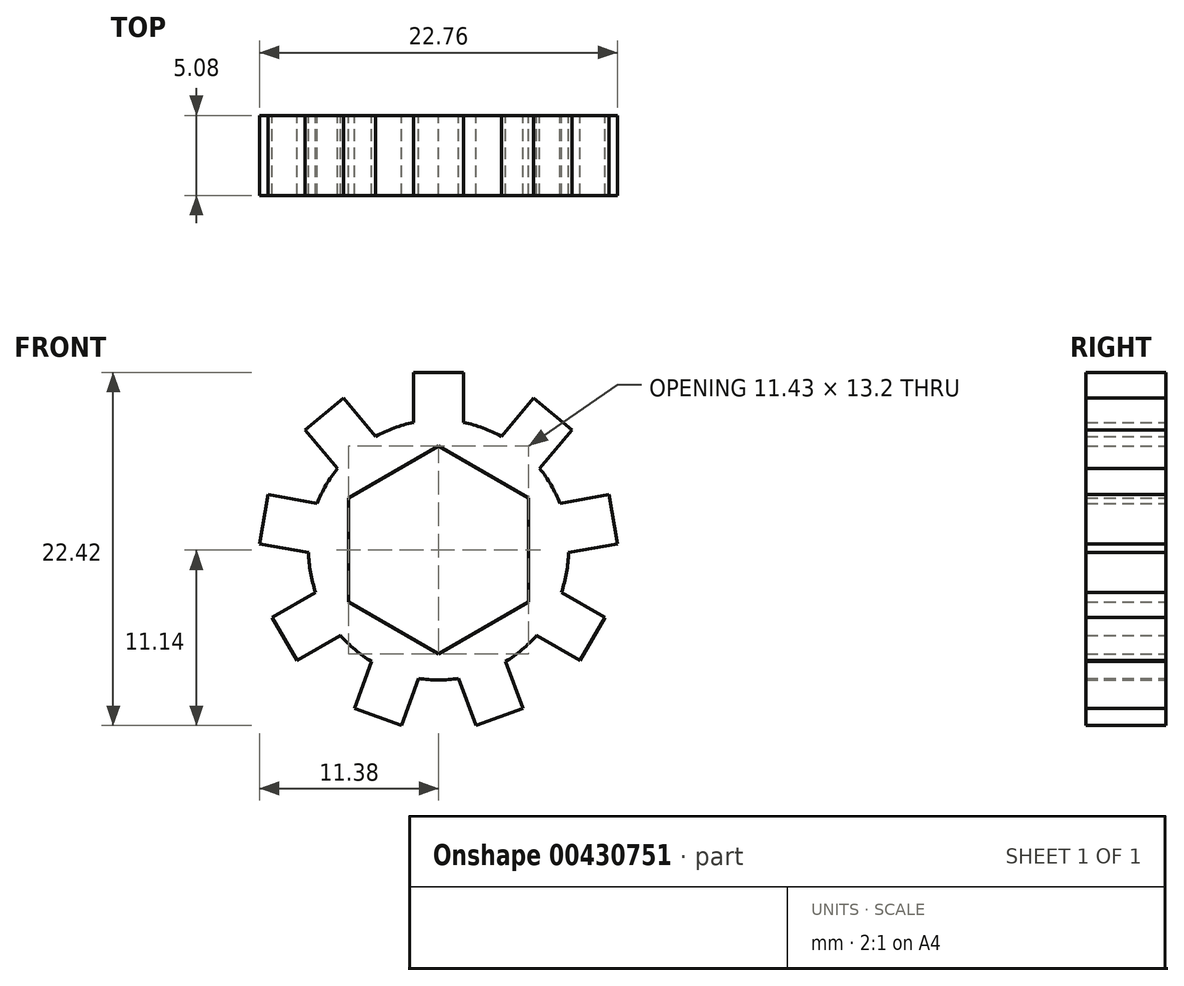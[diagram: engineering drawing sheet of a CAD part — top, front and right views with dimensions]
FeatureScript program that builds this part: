
annotation { "Feature Type Name" : "Feature", "Feature Type Description" : "" }
export const myFeature = defineFeature(function(context is Context, id is Id, definition is map)
    precondition{}
    {
        {
            var Q0;
            Q0=qCreatedBy(makeId("Front.planeOp"),FACE);
            var sketch = newSketch(context, id + "F0", { "sketchPlane" : qUnion([Q0])});
            skCircle(sketch, "E0.cCircle", {"center": v(0, 0) * mm, "radius": 5.72 * mm, "construction": true});
            skLineSegment(sketch, "E0.0", {"start": v(0, 6.6) * mm, "end": v(5.71, 3.3) * mm});
            skLineSegment(sketch, "E0.1", {"start": v(5.71, 3.3) * mm, "end": v(5.72, -3.3) * mm});
            skLineSegment(sketch, "E0.2", {"start": v(5.72, -3.3) * mm, "end": v(0, -6.6) * mm});
            skLineSegment(sketch, "E0.3", {"start": v(0, -6.6) * mm, "end": v(-5.71, -3.3) * mm});
            skLineSegment(sketch, "E0.4", {"start": v(-5.71, -3.3) * mm, "end": v(-5.72, 3.3) * mm});
            skLineSegment(sketch, "E0.5", {"start": v(-5.71, 3.3) * mm, "end": v(0, 6.6) * mm});
            skPoint(sketch, "E0.0.midPoint", {"position": v(2.86, 4.95) * mm});
            skCircle(sketch, "E1", {"center": v(0, 0) * mm, "radius": 8.26 * mm});
            skLineSegment(sketch, "E2", {"start": v(1.59, 8.1) * mm, "end": v(1.59, 11.28) * mm});
            skLineSegment(sketch, "E3", {"start": v(1.59, 11.28) * mm, "end": v(-1.59, 11.28) * mm});
            skLineSegment(sketch, "E4", {"start": v(-1.59, 11.28) * mm, "end": v(-1.59, 8.1) * mm});
            skLineSegment(sketch, "E5.1.0", {"start": v(6.03, 9.66) * mm, "end": v(4, 7.23) * mm});
            skLineSegment(sketch, "E5.1.1", {"start": v(6.42, 5.19) * mm, "end": v(8.46, 7.62) * mm});
            skLineSegment(sketch, "E5.1.2", {"start": v(8.46, 7.62) * mm, "end": v(6.03, 9.66) * mm});
            skLineSegment(sketch, "E5.2.0", {"start": v(10.83, 3.52) * mm, "end": v(7.7, 2.97) * mm});
            skLineSegment(sketch, "E5.2.1", {"start": v(8.25, -0.16) * mm, "end": v(11.38, 0.4) * mm});
            skLineSegment(sketch, "E5.2.2", {"start": v(11.38, 0.4) * mm, "end": v(10.83, 3.52) * mm});
            skLineSegment(sketch, "E5.3.0", {"start": v(10.56, -4.26) * mm, "end": v(7.8, -2.68) * mm});
            skLineSegment(sketch, "E5.3.1", {"start": v(6.22, -5.43) * mm, "end": v(8.97, -7.01) * mm});
            skLineSegment(sketch, "E5.3.2", {"start": v(8.97, -7.01) * mm, "end": v(10.56, -4.26) * mm});
            skLineSegment(sketch, "E5.4.0", {"start": v(5.35, -10.05) * mm, "end": v(4.26, -7.07) * mm});
            skLineSegment(sketch, "E5.4.1", {"start": v(1.28, -8.16) * mm, "end": v(2.36, -11.14) * mm});
            skLineSegment(sketch, "E5.4.2", {"start": v(2.36, -11.14) * mm, "end": v(5.35, -10.05) * mm});
            skLineSegment(sketch, "E5.5.0", {"start": v(-2.36, -11.14) * mm, "end": v(-1.28, -8.16) * mm});
            skLineSegment(sketch, "E5.5.1", {"start": v(-4.26, -7.07) * mm, "end": v(-5.35, -10.05) * mm});
            skLineSegment(sketch, "E5.5.2", {"start": v(-5.35, -10.05) * mm, "end": v(-2.36, -11.14) * mm});
            skLineSegment(sketch, "E5.6.0", {"start": v(-8.97, -7.01) * mm, "end": v(-6.22, -5.43) * mm});
            skLineSegment(sketch, "E5.6.1", {"start": v(-7.8, -2.68) * mm, "end": v(-10.56, -4.26) * mm});
            skLineSegment(sketch, "E5.6.2", {"start": v(-10.56, -4.26) * mm, "end": v(-8.97, -7.01) * mm});
            skLineSegment(sketch, "E5.7.0", {"start": v(-11.38, 0.4) * mm, "end": v(-8.25, -0.16) * mm});
            skLineSegment(sketch, "E5.7.1", {"start": v(-7.7, 2.97) * mm, "end": v(-10.83, 3.52) * mm});
            skLineSegment(sketch, "E5.7.2", {"start": v(-10.83, 3.52) * mm, "end": v(-11.38, 0.4) * mm});
            skLineSegment(sketch, "E5.8.0", {"start": v(-8.46, 7.62) * mm, "end": v(-6.42, 5.19) * mm});
            skLineSegment(sketch, "E5.8.1", {"start": v(-4, 7.23) * mm, "end": v(-6.03, 9.66) * mm});
            skLineSegment(sketch, "E5.8.2", {"start": v(-6.03, 9.66) * mm, "end": v(-8.46, 7.62) * mm});
            skLineSegment(sketch, "E5.anchor1", {"start": v(0, 0) * mm, "end": v(-1.59, 8.1) * mm, "construction": true});
            skLineSegment(sketch, "E5.anchor2", {"start": v(0, 0) * mm, "end": v(-1.59, 8.1) * mm, "construction": true});
            skSolve(sketch);
        }
        {
            var Q0;
            Q0=makeQuery(id+"F0.imprint","IMPRINT",FACE,{"disambiguationData":[TD([[makeQuery(id+"F0.imprint","IMPRINT",EDGE,{"derivedFrom":sQuery(id+"F0.wireOp",EDGE,"E0.0")}),1.0]])]});
            var Q1;
            {var subQ0=sQuery(id+"F0.wireOp",EDGE,"E4");Q1=makeQuery(id+"F0.imprint","IMPRINT",FACE,{"disambiguationData":[TD([[makeQuery(id+"F0.imprint","IMPRINT",EDGE,{"derivedFrom":subQ0}),1.0]])]});}
            var Q2;
            {var subQ0=sQuery(id+"F0.wireOp",EDGE,"E5.1.0");Q2=makeQuery(id+"F0.imprint","IMPRINT",FACE,{"disambiguationData":[TD([[makeQuery(id+"F0.imprint","IMPRINT",EDGE,{"derivedFrom":subQ0}),1.0]])]});}
            var Q3;
            {var subQ0=sQuery(id+"F0.wireOp",EDGE,"E5.2.0");Q3=makeQuery(id+"F0.imprint","IMPRINT",FACE,{"disambiguationData":[TD([[makeQuery(id+"F0.imprint","IMPRINT",EDGE,{"derivedFrom":subQ0}),1.0]])]});}
            var Q4;
            {var subQ0=sQuery(id+"F0.wireOp",EDGE,"E5.3.0");Q4=makeQuery(id+"F0.imprint","IMPRINT",FACE,{"disambiguationData":[TD([[makeQuery(id+"F0.imprint","IMPRINT",EDGE,{"derivedFrom":subQ0}),1.0]])]});}
            var Q5;
            {var subQ0=sQuery(id+"F0.wireOp",EDGE,"E5.4.0");Q5=makeQuery(id+"F0.imprint","IMPRINT",FACE,{"disambiguationData":[TD([[makeQuery(id+"F0.imprint","IMPRINT",EDGE,{"derivedFrom":subQ0}),1.0]])]});}
            var Q6;
            {var subQ0=sQuery(id+"F0.wireOp",EDGE,"E5.5.0");Q6=makeQuery(id+"F0.imprint","IMPRINT",FACE,{"disambiguationData":[TD([[makeQuery(id+"F0.imprint","IMPRINT",EDGE,{"derivedFrom":subQ0}),1.0]])]});}
            var Q7;
            {var subQ0=sQuery(id+"F0.wireOp",EDGE,"E5.6.0");Q7=makeQuery(id+"F0.imprint","IMPRINT",FACE,{"disambiguationData":[TD([[makeQuery(id+"F0.imprint","IMPRINT",EDGE,{"derivedFrom":subQ0}),1.0]])]});}
            var Q8;
            {var subQ0=sQuery(id+"F0.wireOp",EDGE,"E5.7.0");Q8=makeQuery(id+"F0.imprint","IMPRINT",FACE,{"disambiguationData":[TD([[makeQuery(id+"F0.imprint","IMPRINT",EDGE,{"derivedFrom":subQ0}),1.0]])]});}
            var Q9;
            {var subQ0=sQuery(id+"F0.wireOp",EDGE,"E5.8.0");Q9=makeQuery(id+"F0.imprint","IMPRINT",FACE,{"disambiguationData":[TD([[makeQuery(id+"F0.imprint","IMPRINT",EDGE,{"derivedFrom":subQ0}),1.0]])]});}
            extrude(context, id + "F1", {"entities" : qUnion([Q0, Q1, Q2, Q3, Q4, Q5, Q6, Q7, Q8, Q9]), "depth" : 5.08 * mm, "offsetDistance" : 25.4 * mm});
        }
    });
